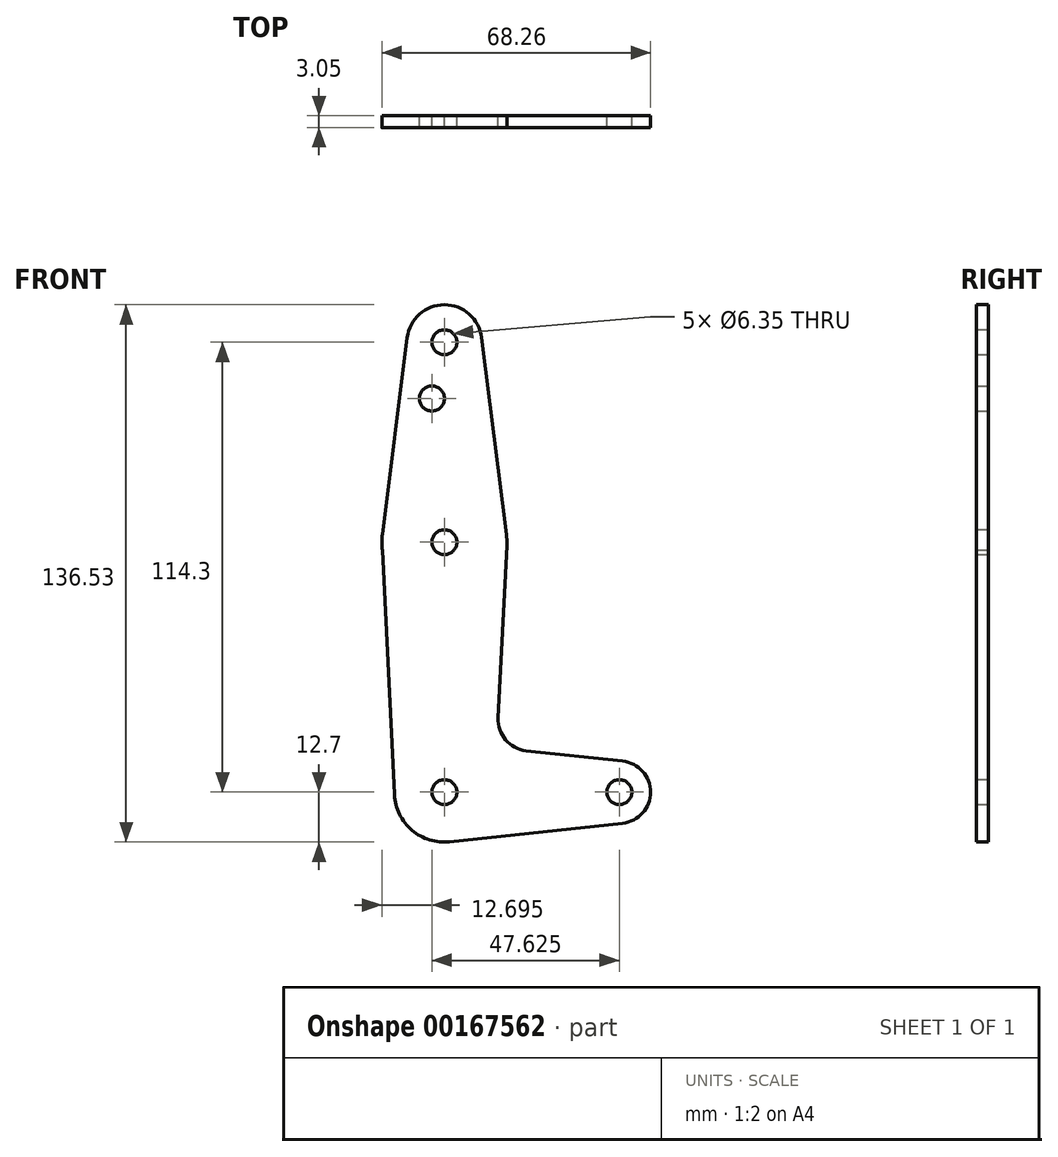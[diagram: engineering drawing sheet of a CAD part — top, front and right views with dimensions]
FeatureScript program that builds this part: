
annotation { "Feature Type Name" : "Feature", "Feature Type Description" : "" }
export const myFeature = defineFeature(function(context is Context, id is Id, definition is map)
    precondition{}
    {
        {
            var Q0;
            Q0=qCreatedBy(makeId("Front.planeOp"),FACE);
            var sketch = newSketch(context, id + "F0", { "sketchPlane" : qUnion([Q0])});
            skLineSegment(sketch, "E0", {"start": v(0, 0) * mm, "end": v(44.45, 0) * mm});
            skLineSegment(sketch, "E1", {"start": v(0, 0) * mm, "end": v(0, 114.3) * mm});
            skCircle(sketch, "E2", {"center": v(0, 114.3) * mm, "radius": 9.53 * mm});
            skCircle(sketch, "E3", {"center": v(0, 63.5) * mm, "radius": 15.88 * mm});
            skCircle(sketch, "E4", {"center": v(0, 0) * mm, "radius": 12.7 * mm});
            skCircle(sketch, "E5", {"center": v(44.45, 0) * mm, "radius": 7.94 * mm});
            skLineSegment(sketch, "E6", {"start": v(-9.45, 115.5) * mm, "end": v(-15.75, 65.48) * mm});
            skLineSegment(sketch, "E7", {"start": v(-15.75, 61.52) * mm, "end": v(-12.68, -0.63) * mm});
            skLineSegment(sketch, "E8", {"start": v(9.45, 115.5) * mm, "end": v(15.75, 65.48) * mm});
            skLineSegment(sketch, "E9", {"start": v(15.86, 62.7) * mm, "end": v(13.66, 18.84) * mm});
            skLineSegment(sketch, "E10", {"start": v(20.75, 10.54) * mm, "end": v(45.3, 7.9) * mm});
            skLineSegment(sketch, "E11", {"start": v(1.36, -12.63) * mm, "end": v(45.3, -7.9) * mm});
            skArc(sketch, "E12.filletArc", {"start": v(13.66, 18.84) * mm, "mid": v(15.55, 13.28) * mm, "end": v(20.75, 10.54) * mm});
            skCircle(sketch, "E13", {"center": v(-3.18, 100.03) * mm, "radius": 3.18 * mm});
            skCircle(sketch, "E14", {"center": v(0, 114.3) * mm, "radius": 3.18 * mm});
            skCircle(sketch, "E15", {"center": v(0, 63.5) * mm, "radius": 3.18 * mm});
            skCircle(sketch, "E16", {"center": v(0, 0) * mm, "radius": 3.18 * mm});
            skCircle(sketch, "E17", {"center": v(44.45, 0) * mm, "radius": 3.18 * mm});
            skSolve(sketch);
        }
        {
            var Q0;
            Q0 = qSketchRegion(id + "F0", true);
            var Q1;
            {var subQ0=sQuery(id+"F0.wireOp",EDGE,"E16");var subQ1=sQuery(id+"F0.wireOp",EDGE,"E0");var subQ2=makeQuery(id+"F0.imprint","INTERSECT",VERTEX,{"derivedFrom":[subQ1,subQ0]});Q1=makeQuery(id+"F0.imprint","IMPRINT",FACE,{"disambiguationData":[TD([[makeQuery(id+"F0.imprint","IMPRINT",EDGE,{"disambiguationData":[TD([[subQ2,-1.0]])],"derivedFrom":subQ1}),1.0]])]});}
            extrude(context, id + "F1", {"entities" : qUnion([Q0, Q1]), "depth" : 3.05 * mm});
        }
    });
